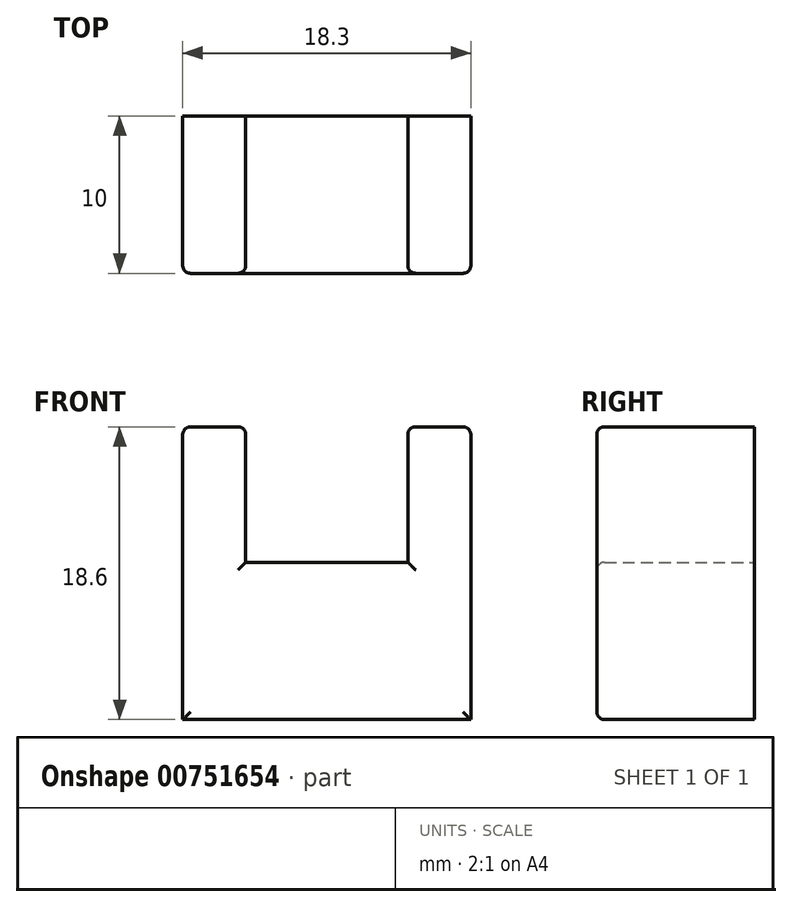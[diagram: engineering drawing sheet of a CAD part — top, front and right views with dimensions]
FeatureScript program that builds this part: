
annotation { "Feature Type Name" : "Feature", "Feature Type Description" : "" }
export const myFeature = defineFeature(function(context is Context, id is Id, definition is map)
    precondition{}
    {
        {
            var Q0;
            Q0=qCreatedBy(makeId("Front.planeOp"),FACE);
            var sketch = newSketch(context, id + "F0", { "sketchPlane" : qUnion([Q0])});
            skLineSegment(sketch, "E0", {"start": v(-9.15, 0) * mm, "end": v(0, 0) * mm});
            skLineSegment(sketch, "E1", {"start": v(-9.15, 0) * mm, "end": v(-9.15, 18.6) * mm});
            skLineSegment(sketch, "E2", {"start": v(-9.15, 18.6) * mm, "end": v(0, 18.6) * mm});
            skLineSegment(sketch, "E3", {"start": v(0, 18.6) * mm, "end": v(0, 0) * mm});
            skLineSegment(sketch, "E4", {"start": v(-5.15, 18.6) * mm, "end": v(-5.15, 10) * mm});
            skLineSegment(sketch, "E5", {"start": v(-5.15, 10) * mm, "end": v(0, 10) * mm});
            skLineSegment(sketch, "E6.MirrorCS", {"start": v(5.15, 10) * mm, "end": v(0, 10) * mm});
            skLineSegment(sketch, "E7.MirrorCS", {"start": v(9.15, 0) * mm, "end": v(0, 0) * mm});
            skLineSegment(sketch, "E8.MirrorCS", {"start": v(9.15, 0) * mm, "end": v(9.15, 18.6) * mm});
            skLineSegment(sketch, "E9.MirrorCS", {"start": v(5.15, 18.6) * mm, "end": v(5.15, 10) * mm});
            skLineSegment(sketch, "E10.MirrorCS", {"start": v(9.15, 18.6) * mm, "end": v(0, 18.6) * mm});
            skSolve(sketch);
        }
        {
            var Q0;
            {var subQ1=sQuery(id+"F0.wireOp",EDGE,"E6.MirrorCS");Q0=makeQuery(id+"F0.imprint","IMPRINT",FACE,{"disambiguationData":[TD([[makeQuery(id+"F0.imprint","IMPRINT",EDGE,{"derivedFrom":subQ1}),1.0]])]});}
            var Q1;
            {var subQ4=sQuery(id+"F0.wireOp",EDGE,"E0");Q1=makeQuery(id+"F0.imprint","IMPRINT",FACE,{"disambiguationData":[TD([[makeQuery(id+"F0.imprint","IMPRINT",EDGE,{"derivedFrom":subQ4}),1.0]])]});}
            extrude(context, id + "F1", {"entities" : qUnion([Q0, Q1]), "depth" : 10 * mm, "offsetDistance" : 25 * mm});
        }
        {
            var Q0;
            Q0=makeQuery(id+"F1.opExtrude","CAP_EDGE",EDGE,{"disambiguationData":[OSD([sQuery(id+"F0.wireOp",EDGE,"E4")])],"isStart":false});
            var Q1;
            Q1=makeQuery(id+"F1.opExtrude","CAP_EDGE",EDGE,{"disambiguationData":[OSD([sQuery(id+"F0.wireOp",EDGE,"E5"),sQuery(id+"F0.wireOp",EDGE,"E6.MirrorCS")])],"isStart":false});
            var Q2;
            Q2=makeQuery(id+"F1.opExtrude","CAP_EDGE",EDGE,{"disambiguationData":[OSD([sQuery(id+"F0.wireOp",EDGE,"E9.MirrorCS")])],"isStart":false});
            var Q3;
            Q3=makeQuery(id+"F1.opExtrude","CAP_EDGE",EDGE,{"disambiguationData":[OSD([sQuery(id+"F0.wireOp",EDGE,"E10.MirrorCS")])],"isStart":false});
            var Q4;
            Q4=makeQuery(id+"F1.opExtrude","CAP_EDGE",EDGE,{"disambiguationData":[OSD([sQuery(id+"F0.wireOp",EDGE,"E8.MirrorCS")])],"isStart":false});
            var Q5;
            Q5=makeQuery(id+"F1.opExtrude","CAP_EDGE",EDGE,{"disambiguationData":[OSD([sQuery(id+"F0.wireOp",EDGE,"E0"),sQuery(id+"F0.wireOp",EDGE,"E7.MirrorCS")])],"isStart":false});
            var Q6;
            Q6=makeQuery(id+"F1.opExtrude","CAP_EDGE",EDGE,{"disambiguationData":[OSD([sQuery(id+"F0.wireOp",EDGE,"E1")])],"isStart":false});
            var Q7;
            Q7=makeQuery(id+"F1.opExtrude","CAP_EDGE",EDGE,{"disambiguationData":[OSD([sQuery(id+"F0.wireOp",EDGE,"E2")])],"isStart":false});
            var Q8;
            Q8=makeQuery(id+"F1.opExtrude","SWEPT_EDGE",EDGE,{"disambiguationData":[OSD([sQuery(id+"F0.wireOp",EDGE,"E9.MirrorCS"),sQuery(id+"F0.wireOp",EDGE,"E10.MirrorCS")])]});
            var Q9;
            Q9=makeQuery(id+"F1.opExtrude","SWEPT_EDGE",EDGE,{"disambiguationData":[OSD([sQuery(id+"F0.wireOp",EDGE,"E8.MirrorCS"),sQuery(id+"F0.wireOp",EDGE,"E10.MirrorCS")])]});
            var Q10;
            Q10=makeQuery(id+"F1.opExtrude","SWEPT_EDGE",EDGE,{"disambiguationData":[OSD([sQuery(id+"F0.wireOp",EDGE,"E2"),sQuery(id+"F0.wireOp",EDGE,"E4")])]});
            var Q11;
            Q11=makeQuery(id+"F1.opExtrude","SWEPT_EDGE",EDGE,{"disambiguationData":[OSD([sQuery(id+"F0.wireOp",EDGE,"E1"),sQuery(id+"F0.wireOp",EDGE,"E2")])]});
            fillet(context, id + "F2", {"entities" : qUnion([Q0, Q1, Q2, Q3, Q4, Q5, Q6, Q7, Q8, Q9, Q10, Q11]), "radius" : 0.5 * mm, "tangentPropagation" : true, "allowEdgeOverflow" : false});
        }
    });
